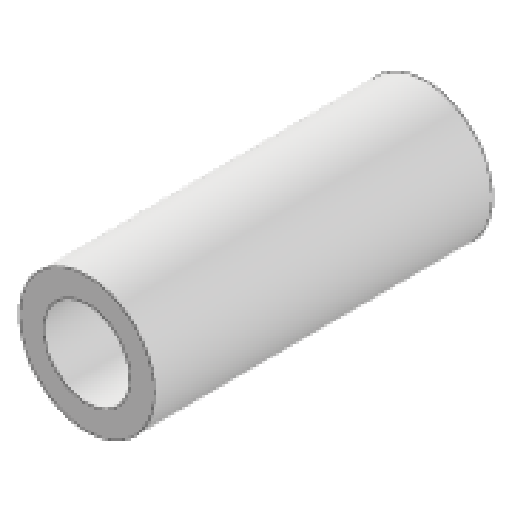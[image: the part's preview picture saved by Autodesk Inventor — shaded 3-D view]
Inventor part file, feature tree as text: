
AUTODESK INVENTOR PART (.ipt)
format: ipt  version: 2025 (Build 290162000, 162)  size: 102,912 bytes
history: native  units: mm
features: extrude x1, sketch x1
ambient origin geometry x8: Origin, YZ Plane, XZ Plane, XY Plane, X Axis, Y Axis, Z Axis, Center Point
bodies: Solid1 (feature_tree)
feature tree (2):
  extrude  "Extrusion1"  Depth=20.0mm
  sketch  "Sketch1"  dims[d0=5.1mm d1=7.99mm d2=20.0mm d3=0.0mm]
